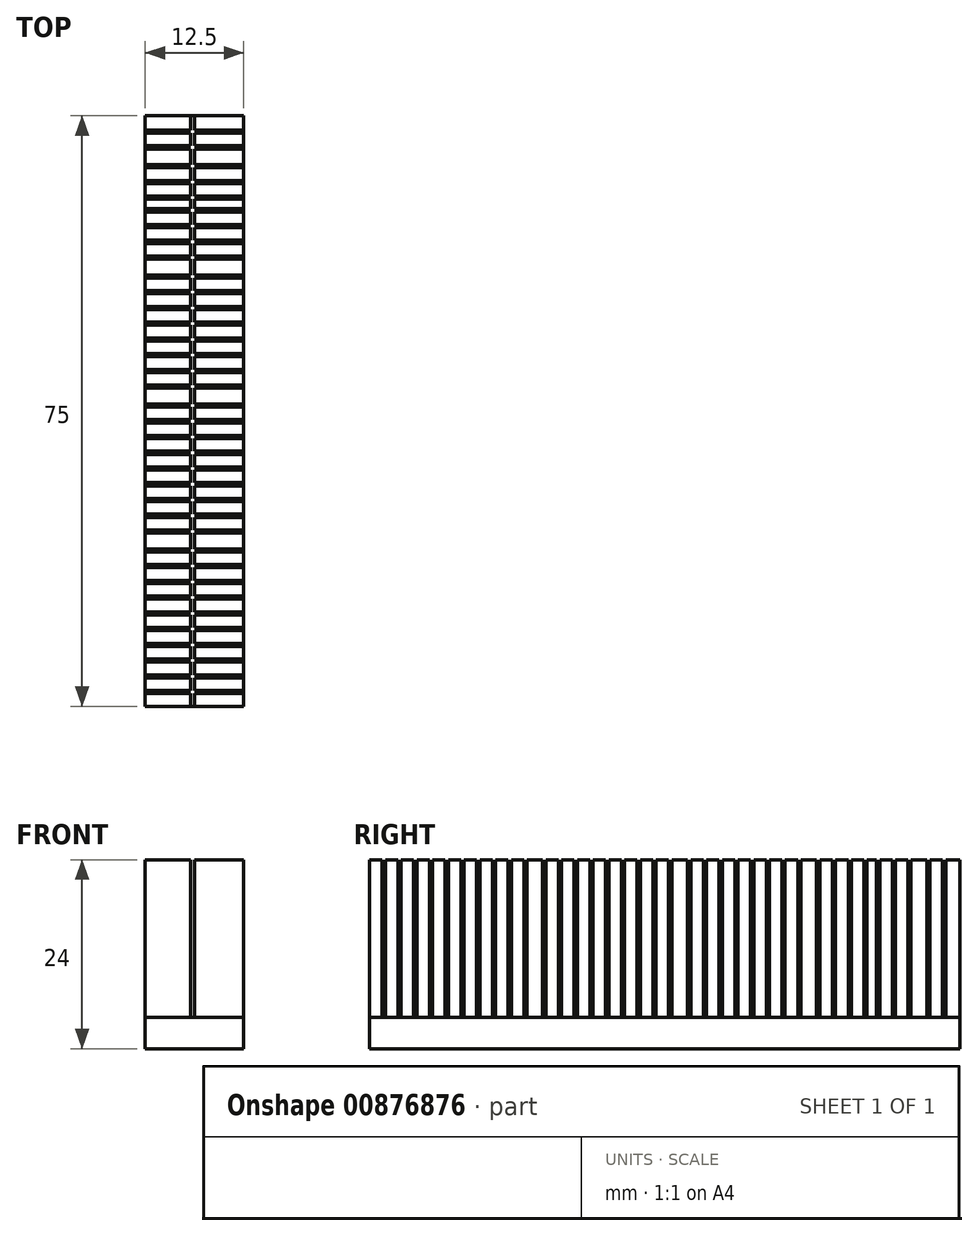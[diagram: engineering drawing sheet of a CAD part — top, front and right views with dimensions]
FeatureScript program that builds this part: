
annotation { "Feature Type Name" : "Feature", "Feature Type Description" : "" }
export const myFeature = defineFeature(function(context is Context, id is Id, definition is map)
    precondition{}
    {
        {
            var Q0;
            Q0=qCreatedBy(makeId("Top.planeOp"),FACE);
            var sketch = newSketch(context, id + "F0", { "sketchPlane" : qUnion([Q0])});
            skLineSegment(sketch, "E0.bottom", {"start": v(6.25, 37.5) * mm, "end": v(-6.25, 37.5) * mm});
            skLineSegment(sketch, "E0.top", {"start": v(6.25, -37.5) * mm, "end": v(-6.25, -37.5) * mm});
            skLineSegment(sketch, "E0.left", {"start": v(6.25, 37.5) * mm, "end": v(6.25, -37.5) * mm});
            skLineSegment(sketch, "E0.right", {"start": v(-6.25, 37.5) * mm, "end": v(-6.25, -37.5) * mm});
            skPoint(sketch, "E0.middle", {"position": v(0, 0) * mm});
            skLineSegment(sketch, "E1", {"start": v(0, -37.5) * mm, "end": v(0, 37.5) * mm});
            skPoint(sketch, "E2", {"position": v(-0.5, -37.5) * mm});
            skLineSegment(sketch, "E3", {"start": v(-0.5, -37.5) * mm, "end": v(-0.5, 37.5) * mm});
            skLineSegment(sketch, "E4", {"start": v(-6.25, -35.9) * mm, "end": v(6.25, -35.9) * mm});
            skLineSegment(sketch, "E5", {"start": v(-6.25, -35.5) * mm, "end": v(6.25, -35.5) * mm});
            skLineSegment(sketch, "E6", {"start": v(-6.25, -33.9) * mm, "end": v(6.25, -33.9) * mm});
            skLineSegment(sketch, "E7", {"start": v(-6.25, -33.5) * mm, "end": v(6.25, -33.5) * mm});
            skLineSegment(sketch, "E8", {"start": v(-6.25, -31.9) * mm, "end": v(6.25, -31.9) * mm});
            skLineSegment(sketch, "E9", {"start": v(-6.25, -31.5) * mm, "end": v(6.25, -31.5) * mm});
            skLineSegment(sketch, "E10", {"start": v(-6.25, -29.9) * mm, "end": v(6.25, -29.9) * mm});
            skLineSegment(sketch, "E11", {"start": v(-6.25, -29.5) * mm, "end": v(6.25, -29.5) * mm});
            skLineSegment(sketch, "E12", {"start": v(-6.25, -25.9) * mm, "end": v(6.25, -25.9) * mm});
            skLineSegment(sketch, "E13", {"start": v(-6.25, -23.5) * mm, "end": v(6.25, -23.5) * mm});
            skLineSegment(sketch, "E14", {"start": v(-6.25, -21.9) * mm, "end": v(6.25, -21.9) * mm});
            skLineSegment(sketch, "E15", {"start": v(-6.25, -21.5) * mm, "end": v(6.25, -21.5) * mm});
            skLineSegment(sketch, "E16", {"start": v(-6.25, -19.9) * mm, "end": v(6.25, -19.9) * mm});
            skLineSegment(sketch, "E17", {"start": v(-6.25, -19.5) * mm, "end": v(6.25, -19.5) * mm});
            skLineSegment(sketch, "E18", {"start": v(-6.25, -17.9) * mm, "end": v(6.25, -17.9) * mm});
            skLineSegment(sketch, "E19", {"start": v(-6.25, -17.5) * mm, "end": v(6.25, -17.5) * mm});
            skLineSegment(sketch, "E20", {"start": v(-6.25, -23.9) * mm, "end": v(6.25, -23.9) * mm});
            skLineSegment(sketch, "E21", {"start": v(-6.25, -25.5) * mm, "end": v(6.25, -25.5) * mm});
            skLineSegment(sketch, "E22", {"start": v(-6.25, -27.5) * mm, "end": v(6.25, -27.5) * mm});
            skLineSegment(sketch, "E23", {"start": v(-6.25, -27.9) * mm, "end": v(6.25, -27.9) * mm});
            skLineSegment(sketch, "E24.MirrorCS", {"start": v(-6.25, -15.1) * mm, "end": v(6.25, -15.1) * mm});
            skLineSegment(sketch, "E25.MirrorCS", {"start": v(-6.25, -15.5) * mm, "end": v(6.25, -15.5) * mm});
            skLineSegment(sketch, "E26.MirrorCS", {"start": v(-6.25, -13.1) * mm, "end": v(6.25, -13.1) * mm});
            skLineSegment(sketch, "E27.MirrorCS", {"start": v(-6.25, -13.5) * mm, "end": v(6.25, -13.5) * mm});
            skLineSegment(sketch, "E28.MirrorCS", {"start": v(-6.25, -11.1) * mm, "end": v(6.25, -11.1) * mm});
            skLineSegment(sketch, "E29.MirrorCS", {"start": v(-6.25, -11.5) * mm, "end": v(6.25, -11.5) * mm});
            skLineSegment(sketch, "E30.MirrorCS", {"start": v(-6.25, -9.1) * mm, "end": v(6.25, -9.1) * mm});
            skLineSegment(sketch, "E31.MirrorCS", {"start": v(-6.25, -9.5) * mm, "end": v(6.25, -9.5) * mm});
            skLineSegment(sketch, "E32.MirrorCS", {"start": v(-6.25, -7.5) * mm, "end": v(6.25, -7.5) * mm});
            skLineSegment(sketch, "E33.MirrorCS", {"start": v(-6.25, -7.1) * mm, "end": v(6.25, -7.1) * mm});
            skLineSegment(sketch, "E34.MirrorCS", {"start": v(-6.25, -5.5) * mm, "end": v(6.25, -5.5) * mm});
            skLineSegment(sketch, "E35.MirrorCS", {"start": v(-6.25, -5.1) * mm, "end": v(6.25, -5.1) * mm});
            skLineSegment(sketch, "E36.MirrorCS", {"start": v(-6.25, -3.5) * mm, "end": v(6.25, -3.5) * mm});
            skLineSegment(sketch, "E37.MirrorCS", {"start": v(-6.25, -3.1) * mm, "end": v(6.25, -3.1) * mm});
            skLineSegment(sketch, "E38.MirrorCS", {"start": v(-6.25, -1.1) * mm, "end": v(6.25, -1.1) * mm});
            skLineSegment(sketch, "E39.MirrorCS", {"start": v(-6.25, -1.5) * mm, "end": v(6.25, -1.5) * mm});
            skLineSegment(sketch, "E40.MirrorCS", {"start": v(-6.25, 0.5) * mm, "end": v(6.25, 0.5) * mm});
            skLineSegment(sketch, "E41.MirrorCS", {"start": v(-6.25, 0.9) * mm, "end": v(6.25, 0.9) * mm});
            skLineSegment(sketch, "E42.MirrorCS", {"start": v(-6.25, 2.9) * mm, "end": v(6.25, 2.9) * mm});
            skLineSegment(sketch, "E43.MirrorCS", {"start": v(-6.25, 3.3) * mm, "end": v(6.25, 3.3) * mm});
            skLineSegment(sketch, "E44.MirrorCS", {"start": v(-6.25, 5.3) * mm, "end": v(6.25, 5.3) * mm});
            skLineSegment(sketch, "E45.MirrorCS", {"start": v(-6.25, 4.9) * mm, "end": v(6.25, 4.9) * mm});
            skLineSegment(sketch, "E46.MirrorCS", {"start": v(-6.25, 6.9) * mm, "end": v(6.25, 6.9) * mm});
            skLineSegment(sketch, "E47.MirrorCS", {"start": v(-6.25, 7.3) * mm, "end": v(6.25, 7.3) * mm});
            skLineSegment(sketch, "E48.MirrorCS", {"start": v(-6.25, 8.9) * mm, "end": v(6.25, 8.9) * mm});
            skLineSegment(sketch, "E49.MirrorCS", {"start": v(-6.25, 9.3) * mm, "end": v(6.25, 9.3) * mm});
            skLineSegment(sketch, "E50.MirrorCS", {"start": v(-6.25, 10.9) * mm, "end": v(6.25, 10.9) * mm});
            skLineSegment(sketch, "E51.MirrorCS", {"start": v(-6.25, 11.3) * mm, "end": v(6.25, 11.3) * mm});
            skLineSegment(sketch, "E52.MirrorCS", {"start": v(-6.25, 12.9) * mm, "end": v(6.25, 12.9) * mm});
            skLineSegment(sketch, "E53.MirrorCS", {"start": v(-6.25, 13.3) * mm, "end": v(6.25, 13.3) * mm});
            skLineSegment(sketch, "E54.MirrorCS", {"start": v(-6.25, 14.9) * mm, "end": v(6.25, 14.9) * mm});
            skLineSegment(sketch, "E55.MirrorCS", {"start": v(-6.25, 15.3) * mm, "end": v(6.25, 15.3) * mm});
            skLineSegment(sketch, "E56.MirrorCS", {"start": v(-6.25, 16.9) * mm, "end": v(6.25, 16.9) * mm});
            skLineSegment(sketch, "E57.MirrorCS", {"start": v(-6.25, 17.3) * mm, "end": v(6.25, 17.3) * mm});
            skLineSegment(sketch, "E58.MirrorCS", {"start": v(-6.25, 19.7) * mm, "end": v(6.25, 19.7) * mm});
            skLineSegment(sketch, "E59.MirrorCS", {"start": v(-6.25, 19.3) * mm, "end": v(6.25, 19.3) * mm});
            skLineSegment(sketch, "E60.MirrorCS", {"start": v(-6.25, 21.3) * mm, "end": v(6.25, 21.3) * mm});
            skLineSegment(sketch, "E61.MirrorCS", {"start": v(-6.25, 21.7) * mm, "end": v(6.25, 21.7) * mm});
            skLineSegment(sketch, "E62.MirrorCS", {"start": v(-6.25, 23.3) * mm, "end": v(6.25, 23.3) * mm});
            skLineSegment(sketch, "E63.MirrorCS", {"start": v(-6.25, 23.7) * mm, "end": v(6.25, 23.7) * mm});
            skLineSegment(sketch, "E64.MirrorCS", {"start": v(-6.25, 25.7) * mm, "end": v(6.25, 25.7) * mm});
            skLineSegment(sketch, "E65.MirrorCS", {"start": v(-6.25, 25.3) * mm, "end": v(6.25, 25.3) * mm});
            skLineSegment(sketch, "E66.MirrorCS", {"start": v(-6.25, 26.9) * mm, "end": v(6.25, 26.9) * mm});
            skLineSegment(sketch, "E67.MirrorCS", {"start": v(-6.25, 27.3) * mm, "end": v(6.25, 27.3) * mm});
            skLineSegment(sketch, "E68.MirrorCS", {"start": v(-6.25, 28.9) * mm, "end": v(6.25, 28.9) * mm});
            skLineSegment(sketch, "E69.MirrorCS", {"start": v(-6.25, 29.3) * mm, "end": v(6.25, 29.3) * mm});
            skLineSegment(sketch, "E70.MirrorCS", {"start": v(-6.25, 30.9) * mm, "end": v(6.25, 30.9) * mm});
            skLineSegment(sketch, "E71.MirrorCS", {"start": v(-6.25, 31.3) * mm, "end": v(6.25, 31.3) * mm});
            skLineSegment(sketch, "E72.MirrorCS", {"start": v(-6.25, 33.3) * mm, "end": v(6.25, 33.3) * mm});
            skLineSegment(sketch, "E73.MirrorCS", {"start": v(-6.25, 33.7) * mm, "end": v(6.25, 33.7) * mm});
            skLineSegment(sketch, "E74.MirrorCS", {"start": v(-6.25, 35.7) * mm, "end": v(6.25, 35.7) * mm});
            skLineSegment(sketch, "E75.MirrorCS", {"start": v(-6.25, 35.3) * mm, "end": v(6.25, 35.3) * mm});
            skSolve(sketch);
        }
        {
            var Q0;
            {var subQ0=sQuery(id+"F0.wireOp",EDGE,"E0.left");var subQ1=sQuery(id+"F0.wireOp",EDGE,"E0.bottom");var subQ2=makeQuery(id+"F0.imprint","INTERSECT",VERTEX,{"derivedFrom":[subQ1,subQ0]});Q0=makeQuery(id+"F0.imprint","IMPRINT",FACE,{"disambiguationData":[TD([[makeQuery(id+"F0.imprint","IMPRINT",EDGE,{"disambiguationData":[TD([[subQ2,-1.0]])],"derivedFrom":subQ1}),1.0]])]});}
            var Q1;
            {var subQ0=sQuery(id+"F0.wireOp",EDGE,"E0.right");var subQ1=sQuery(id+"F0.wireOp",EDGE,"E0.bottom");var subQ2=makeQuery(id+"F0.imprint","INTERSECT",VERTEX,{"derivedFrom":[subQ1,subQ0]});Q1=makeQuery(id+"F0.imprint","IMPRINT",FACE,{"disambiguationData":[TD([[makeQuery(id+"F0.imprint","IMPRINT",EDGE,{"disambiguationData":[TD([[subQ2,1.0]])],"derivedFrom":subQ1}),1.0]])]});}
            var Q2;
            {var subQ0=sQuery(id+"F0.wireOp",EDGE,"E73.MirrorCS");var subQ1=sQuery(id+"F0.wireOp",EDGE,"E0.left");var subQ2=makeQuery(id+"F0.imprint","INTERSECT",VERTEX,{"derivedFrom":[subQ1,subQ0]});Q2=makeQuery(id+"F0.imprint","IMPRINT",FACE,{"disambiguationData":[TD([[makeQuery(id+"F0.imprint","IMPRINT",EDGE,{"disambiguationData":[TD([[subQ2,1.0]])],"derivedFrom":subQ1}),-1.0]])]});}
            var Q3;
            {var subQ0=sQuery(id+"F0.wireOp",EDGE,"E73.MirrorCS");var subQ1=sQuery(id+"F0.wireOp",EDGE,"E0.right");var subQ2=makeQuery(id+"F0.imprint","INTERSECT",VERTEX,{"derivedFrom":[subQ1,subQ0]});Q3=makeQuery(id+"F0.imprint","IMPRINT",FACE,{"disambiguationData":[TD([[makeQuery(id+"F0.imprint","IMPRINT",EDGE,{"disambiguationData":[TD([[subQ2,1.0]])],"derivedFrom":subQ1}),1.0]])]});}
            var Q4;
            {var subQ0=sQuery(id+"F0.wireOp",EDGE,"E71.MirrorCS");var subQ1=sQuery(id+"F0.wireOp",EDGE,"E0.left");var subQ2=makeQuery(id+"F0.imprint","INTERSECT",VERTEX,{"derivedFrom":[subQ1,subQ0]});Q4=makeQuery(id+"F0.imprint","IMPRINT",FACE,{"disambiguationData":[TD([[makeQuery(id+"F0.imprint","IMPRINT",EDGE,{"disambiguationData":[TD([[subQ2,1.0]])],"derivedFrom":subQ1}),-1.0]])]});}
            var Q5;
            {var subQ0=sQuery(id+"F0.wireOp",EDGE,"E71.MirrorCS");var subQ1=sQuery(id+"F0.wireOp",EDGE,"E0.right");var subQ2=makeQuery(id+"F0.imprint","INTERSECT",VERTEX,{"derivedFrom":[subQ1,subQ0]});Q5=makeQuery(id+"F0.imprint","IMPRINT",FACE,{"disambiguationData":[TD([[makeQuery(id+"F0.imprint","IMPRINT",EDGE,{"disambiguationData":[TD([[subQ2,1.0]])],"derivedFrom":subQ1}),1.0]])]});}
            var Q6;
            {var subQ0=sQuery(id+"F0.wireOp",EDGE,"E69.MirrorCS");var subQ1=sQuery(id+"F0.wireOp",EDGE,"E0.right");var subQ2=makeQuery(id+"F0.imprint","INTERSECT",VERTEX,{"derivedFrom":[subQ1,subQ0]});Q6=makeQuery(id+"F0.imprint","IMPRINT",FACE,{"disambiguationData":[TD([[makeQuery(id+"F0.imprint","IMPRINT",EDGE,{"disambiguationData":[TD([[subQ2,1.0]])],"derivedFrom":subQ1}),1.0]])]});}
            var Q7;
            {var subQ0=sQuery(id+"F0.wireOp",EDGE,"E69.MirrorCS");var subQ1=sQuery(id+"F0.wireOp",EDGE,"E0.left");var subQ2=makeQuery(id+"F0.imprint","INTERSECT",VERTEX,{"derivedFrom":[subQ1,subQ0]});Q7=makeQuery(id+"F0.imprint","IMPRINT",FACE,{"disambiguationData":[TD([[makeQuery(id+"F0.imprint","IMPRINT",EDGE,{"disambiguationData":[TD([[subQ2,1.0]])],"derivedFrom":subQ1}),-1.0]])]});}
            var Q8;
            {var subQ0=sQuery(id+"F0.wireOp",EDGE,"E67.MirrorCS");var subQ1=sQuery(id+"F0.wireOp",EDGE,"E0.left");var subQ2=makeQuery(id+"F0.imprint","INTERSECT",VERTEX,{"derivedFrom":[subQ1,subQ0]});Q8=makeQuery(id+"F0.imprint","IMPRINT",FACE,{"disambiguationData":[TD([[makeQuery(id+"F0.imprint","IMPRINT",EDGE,{"disambiguationData":[TD([[subQ2,1.0]])],"derivedFrom":subQ1}),-1.0]])]});}
            var Q9;
            {var subQ0=sQuery(id+"F0.wireOp",EDGE,"E67.MirrorCS");var subQ1=sQuery(id+"F0.wireOp",EDGE,"E0.right");var subQ2=makeQuery(id+"F0.imprint","INTERSECT",VERTEX,{"derivedFrom":[subQ1,subQ0]});Q9=makeQuery(id+"F0.imprint","IMPRINT",FACE,{"disambiguationData":[TD([[makeQuery(id+"F0.imprint","IMPRINT",EDGE,{"disambiguationData":[TD([[subQ2,1.0]])],"derivedFrom":subQ1}),1.0]])]});}
            var Q10;
            {var subQ0=sQuery(id+"F0.wireOp",EDGE,"E64.MirrorCS");var subQ1=sQuery(id+"F0.wireOp",EDGE,"E0.right");var subQ2=makeQuery(id+"F0.imprint","INTERSECT",VERTEX,{"derivedFrom":[subQ1,subQ0]});Q10=makeQuery(id+"F0.imprint","IMPRINT",FACE,{"disambiguationData":[TD([[makeQuery(id+"F0.imprint","IMPRINT",EDGE,{"disambiguationData":[TD([[subQ2,1.0]])],"derivedFrom":subQ1}),1.0]])]});}
            var Q11;
            {var subQ0=sQuery(id+"F0.wireOp",EDGE,"E64.MirrorCS");var subQ1=sQuery(id+"F0.wireOp",EDGE,"E0.left");var subQ2=makeQuery(id+"F0.imprint","INTERSECT",VERTEX,{"derivedFrom":[subQ1,subQ0]});Q11=makeQuery(id+"F0.imprint","IMPRINT",FACE,{"disambiguationData":[TD([[makeQuery(id+"F0.imprint","IMPRINT",EDGE,{"disambiguationData":[TD([[subQ2,1.0]])],"derivedFrom":subQ1}),-1.0]])]});}
            var Q12;
            {var subQ0=sQuery(id+"F0.wireOp",EDGE,"E63.MirrorCS");var subQ1=sQuery(id+"F0.wireOp",EDGE,"E0.right");var subQ2=makeQuery(id+"F0.imprint","INTERSECT",VERTEX,{"derivedFrom":[subQ1,subQ0]});Q12=makeQuery(id+"F0.imprint","IMPRINT",FACE,{"disambiguationData":[TD([[makeQuery(id+"F0.imprint","IMPRINT",EDGE,{"disambiguationData":[TD([[subQ2,1.0]])],"derivedFrom":subQ1}),1.0]])]});}
            var Q13;
            {var subQ0=sQuery(id+"F0.wireOp",EDGE,"E63.MirrorCS");var subQ1=sQuery(id+"F0.wireOp",EDGE,"E0.left");var subQ2=makeQuery(id+"F0.imprint","INTERSECT",VERTEX,{"derivedFrom":[subQ1,subQ0]});Q13=makeQuery(id+"F0.imprint","IMPRINT",FACE,{"disambiguationData":[TD([[makeQuery(id+"F0.imprint","IMPRINT",EDGE,{"disambiguationData":[TD([[subQ2,1.0]])],"derivedFrom":subQ1}),-1.0]])]});}
            var Q14;
            {var subQ0=sQuery(id+"F0.wireOp",EDGE,"E61.MirrorCS");var subQ1=sQuery(id+"F0.wireOp",EDGE,"E0.right");var subQ2=makeQuery(id+"F0.imprint","INTERSECT",VERTEX,{"derivedFrom":[subQ1,subQ0]});Q14=makeQuery(id+"F0.imprint","IMPRINT",FACE,{"disambiguationData":[TD([[makeQuery(id+"F0.imprint","IMPRINT",EDGE,{"disambiguationData":[TD([[subQ2,1.0]])],"derivedFrom":subQ1}),1.0]])]});}
            var Q15;
            {var subQ0=sQuery(id+"F0.wireOp",EDGE,"E61.MirrorCS");var subQ1=sQuery(id+"F0.wireOp",EDGE,"E0.left");var subQ2=makeQuery(id+"F0.imprint","INTERSECT",VERTEX,{"derivedFrom":[subQ1,subQ0]});Q15=makeQuery(id+"F0.imprint","IMPRINT",FACE,{"disambiguationData":[TD([[makeQuery(id+"F0.imprint","IMPRINT",EDGE,{"disambiguationData":[TD([[subQ2,1.0]])],"derivedFrom":subQ1}),-1.0]])]});}
            var Q16;
            {var subQ0=sQuery(id+"F0.wireOp",EDGE,"E60.MirrorCS");var subQ1=sQuery(id+"F0.wireOp",EDGE,"E0.right");var subQ2=makeQuery(id+"F0.imprint","INTERSECT",VERTEX,{"derivedFrom":[subQ1,subQ0]});Q16=makeQuery(id+"F0.imprint","IMPRINT",FACE,{"disambiguationData":[TD([[makeQuery(id+"F0.imprint","IMPRINT",EDGE,{"disambiguationData":[TD([[subQ2,-1.0]])],"derivedFrom":subQ1}),1.0]])]});}
            var Q17;
            {var subQ0=sQuery(id+"F0.wireOp",EDGE,"E60.MirrorCS");var subQ1=sQuery(id+"F0.wireOp",EDGE,"E0.left");var subQ2=makeQuery(id+"F0.imprint","INTERSECT",VERTEX,{"derivedFrom":[subQ1,subQ0]});Q17=makeQuery(id+"F0.imprint","IMPRINT",FACE,{"disambiguationData":[TD([[makeQuery(id+"F0.imprint","IMPRINT",EDGE,{"disambiguationData":[TD([[subQ2,-1.0]])],"derivedFrom":subQ1}),-1.0]])]});}
            var Q18;
            {var subQ0=sQuery(id+"F0.wireOp",EDGE,"E57.MirrorCS");var subQ1=sQuery(id+"F0.wireOp",EDGE,"E0.right");var subQ2=makeQuery(id+"F0.imprint","INTERSECT",VERTEX,{"derivedFrom":[subQ1,subQ0]});Q18=makeQuery(id+"F0.imprint","IMPRINT",FACE,{"disambiguationData":[TD([[makeQuery(id+"F0.imprint","IMPRINT",EDGE,{"disambiguationData":[TD([[subQ2,1.0]])],"derivedFrom":subQ1}),1.0]])]});}
            var Q19;
            {var subQ0=sQuery(id+"F0.wireOp",EDGE,"E57.MirrorCS");var subQ1=sQuery(id+"F0.wireOp",EDGE,"E0.left");var subQ2=makeQuery(id+"F0.imprint","INTERSECT",VERTEX,{"derivedFrom":[subQ1,subQ0]});Q19=makeQuery(id+"F0.imprint","IMPRINT",FACE,{"disambiguationData":[TD([[makeQuery(id+"F0.imprint","IMPRINT",EDGE,{"disambiguationData":[TD([[subQ2,1.0]])],"derivedFrom":subQ1}),-1.0]])]});}
            var Q20;
            {var subQ0=sQuery(id+"F0.wireOp",EDGE,"E55.MirrorCS");var subQ1=sQuery(id+"F0.wireOp",EDGE,"E0.left");var subQ2=makeQuery(id+"F0.imprint","INTERSECT",VERTEX,{"derivedFrom":[subQ1,subQ0]});Q20=makeQuery(id+"F0.imprint","IMPRINT",FACE,{"disambiguationData":[TD([[makeQuery(id+"F0.imprint","IMPRINT",EDGE,{"disambiguationData":[TD([[subQ2,1.0]])],"derivedFrom":subQ1}),-1.0]])]});}
            var Q21;
            {var subQ0=sQuery(id+"F0.wireOp",EDGE,"E55.MirrorCS");var subQ1=sQuery(id+"F0.wireOp",EDGE,"E0.right");var subQ2=makeQuery(id+"F0.imprint","INTERSECT",VERTEX,{"derivedFrom":[subQ1,subQ0]});Q21=makeQuery(id+"F0.imprint","IMPRINT",FACE,{"disambiguationData":[TD([[makeQuery(id+"F0.imprint","IMPRINT",EDGE,{"disambiguationData":[TD([[subQ2,1.0]])],"derivedFrom":subQ1}),1.0]])]});}
            var Q22;
            {var subQ0=sQuery(id+"F0.wireOp",EDGE,"E53.MirrorCS");var subQ1=sQuery(id+"F0.wireOp",EDGE,"E0.left");var subQ2=makeQuery(id+"F0.imprint","INTERSECT",VERTEX,{"derivedFrom":[subQ1,subQ0]});Q22=makeQuery(id+"F0.imprint","IMPRINT",FACE,{"disambiguationData":[TD([[makeQuery(id+"F0.imprint","IMPRINT",EDGE,{"disambiguationData":[TD([[subQ2,1.0]])],"derivedFrom":subQ1}),-1.0]])]});}
            var Q23;
            {var subQ0=sQuery(id+"F0.wireOp",EDGE,"E53.MirrorCS");var subQ1=sQuery(id+"F0.wireOp",EDGE,"E0.right");var subQ2=makeQuery(id+"F0.imprint","INTERSECT",VERTEX,{"derivedFrom":[subQ1,subQ0]});Q23=makeQuery(id+"F0.imprint","IMPRINT",FACE,{"disambiguationData":[TD([[makeQuery(id+"F0.imprint","IMPRINT",EDGE,{"disambiguationData":[TD([[subQ2,1.0]])],"derivedFrom":subQ1}),1.0]])]});}
            var Q24;
            {var subQ0=sQuery(id+"F0.wireOp",EDGE,"E51.MirrorCS");var subQ1=sQuery(id+"F0.wireOp",EDGE,"E0.right");var subQ2=makeQuery(id+"F0.imprint","INTERSECT",VERTEX,{"derivedFrom":[subQ1,subQ0]});Q24=makeQuery(id+"F0.imprint","IMPRINT",FACE,{"disambiguationData":[TD([[makeQuery(id+"F0.imprint","IMPRINT",EDGE,{"disambiguationData":[TD([[subQ2,1.0]])],"derivedFrom":subQ1}),1.0]])]});}
            var Q25;
            {var subQ0=sQuery(id+"F0.wireOp",EDGE,"E51.MirrorCS");var subQ1=sQuery(id+"F0.wireOp",EDGE,"E0.left");var subQ2=makeQuery(id+"F0.imprint","INTERSECT",VERTEX,{"derivedFrom":[subQ1,subQ0]});Q25=makeQuery(id+"F0.imprint","IMPRINT",FACE,{"disambiguationData":[TD([[makeQuery(id+"F0.imprint","IMPRINT",EDGE,{"disambiguationData":[TD([[subQ2,1.0]])],"derivedFrom":subQ1}),-1.0]])]});}
            var Q26;
            {var subQ0=sQuery(id+"F0.wireOp",EDGE,"E49.MirrorCS");var subQ1=sQuery(id+"F0.wireOp",EDGE,"E0.right");var subQ2=makeQuery(id+"F0.imprint","INTERSECT",VERTEX,{"derivedFrom":[subQ1,subQ0]});Q26=makeQuery(id+"F0.imprint","IMPRINT",FACE,{"disambiguationData":[TD([[makeQuery(id+"F0.imprint","IMPRINT",EDGE,{"disambiguationData":[TD([[subQ2,1.0]])],"derivedFrom":subQ1}),1.0]])]});}
            var Q27;
            {var subQ0=sQuery(id+"F0.wireOp",EDGE,"E49.MirrorCS");var subQ1=sQuery(id+"F0.wireOp",EDGE,"E0.left");var subQ2=makeQuery(id+"F0.imprint","INTERSECT",VERTEX,{"derivedFrom":[subQ1,subQ0]});Q27=makeQuery(id+"F0.imprint","IMPRINT",FACE,{"disambiguationData":[TD([[makeQuery(id+"F0.imprint","IMPRINT",EDGE,{"disambiguationData":[TD([[subQ2,1.0]])],"derivedFrom":subQ1}),-1.0]])]});}
            var Q28;
            {var subQ0=sQuery(id+"F0.wireOp",EDGE,"E47.MirrorCS");var subQ1=sQuery(id+"F0.wireOp",EDGE,"E0.right");var subQ2=makeQuery(id+"F0.imprint","INTERSECT",VERTEX,{"derivedFrom":[subQ1,subQ0]});Q28=makeQuery(id+"F0.imprint","IMPRINT",FACE,{"disambiguationData":[TD([[makeQuery(id+"F0.imprint","IMPRINT",EDGE,{"disambiguationData":[TD([[subQ2,1.0]])],"derivedFrom":subQ1}),1.0]])]});}
            var Q29;
            {var subQ0=sQuery(id+"F0.wireOp",EDGE,"E47.MirrorCS");var subQ1=sQuery(id+"F0.wireOp",EDGE,"E0.left");var subQ2=makeQuery(id+"F0.imprint","INTERSECT",VERTEX,{"derivedFrom":[subQ1,subQ0]});Q29=makeQuery(id+"F0.imprint","IMPRINT",FACE,{"disambiguationData":[TD([[makeQuery(id+"F0.imprint","IMPRINT",EDGE,{"disambiguationData":[TD([[subQ2,1.0]])],"derivedFrom":subQ1}),-1.0]])]});}
            var Q30;
            {var subQ0=sQuery(id+"F0.wireOp",EDGE,"E44.MirrorCS");var subQ1=sQuery(id+"F0.wireOp",EDGE,"E0.left");var subQ2=makeQuery(id+"F0.imprint","INTERSECT",VERTEX,{"derivedFrom":[subQ1,subQ0]});Q30=makeQuery(id+"F0.imprint","IMPRINT",FACE,{"disambiguationData":[TD([[makeQuery(id+"F0.imprint","IMPRINT",EDGE,{"disambiguationData":[TD([[subQ2,1.0]])],"derivedFrom":subQ1}),-1.0]])]});}
            var Q31;
            {var subQ0=sQuery(id+"F0.wireOp",EDGE,"E44.MirrorCS");var subQ1=sQuery(id+"F0.wireOp",EDGE,"E0.right");var subQ2=makeQuery(id+"F0.imprint","INTERSECT",VERTEX,{"derivedFrom":[subQ1,subQ0]});Q31=makeQuery(id+"F0.imprint","IMPRINT",FACE,{"disambiguationData":[TD([[makeQuery(id+"F0.imprint","IMPRINT",EDGE,{"disambiguationData":[TD([[subQ2,1.0]])],"derivedFrom":subQ1}),1.0]])]});}
            var Q32;
            {var subQ0=sQuery(id+"F0.wireOp",EDGE,"E43.MirrorCS");var subQ1=sQuery(id+"F0.wireOp",EDGE,"E0.right");var subQ2=makeQuery(id+"F0.imprint","INTERSECT",VERTEX,{"derivedFrom":[subQ1,subQ0]});Q32=makeQuery(id+"F0.imprint","IMPRINT",FACE,{"disambiguationData":[TD([[makeQuery(id+"F0.imprint","IMPRINT",EDGE,{"disambiguationData":[TD([[subQ2,1.0]])],"derivedFrom":subQ1}),1.0]])]});}
            var Q33;
            {var subQ0=sQuery(id+"F0.wireOp",EDGE,"E43.MirrorCS");var subQ1=sQuery(id+"F0.wireOp",EDGE,"E0.left");var subQ2=makeQuery(id+"F0.imprint","INTERSECT",VERTEX,{"derivedFrom":[subQ1,subQ0]});Q33=makeQuery(id+"F0.imprint","IMPRINT",FACE,{"disambiguationData":[TD([[makeQuery(id+"F0.imprint","IMPRINT",EDGE,{"disambiguationData":[TD([[subQ2,1.0]])],"derivedFrom":subQ1}),-1.0]])]});}
            var Q34;
            {var subQ0=sQuery(id+"F0.wireOp",EDGE,"E41.MirrorCS");var subQ1=sQuery(id+"F0.wireOp",EDGE,"E0.left");var subQ2=makeQuery(id+"F0.imprint","INTERSECT",VERTEX,{"derivedFrom":[subQ1,subQ0]});Q34=makeQuery(id+"F0.imprint","IMPRINT",FACE,{"disambiguationData":[TD([[makeQuery(id+"F0.imprint","IMPRINT",EDGE,{"disambiguationData":[TD([[subQ2,1.0]])],"derivedFrom":subQ1}),-1.0]])]});}
            var Q35;
            {var subQ0=sQuery(id+"F0.wireOp",EDGE,"E41.MirrorCS");var subQ1=sQuery(id+"F0.wireOp",EDGE,"E0.right");var subQ2=makeQuery(id+"F0.imprint","INTERSECT",VERTEX,{"derivedFrom":[subQ1,subQ0]});Q35=makeQuery(id+"F0.imprint","IMPRINT",FACE,{"disambiguationData":[TD([[makeQuery(id+"F0.imprint","IMPRINT",EDGE,{"disambiguationData":[TD([[subQ2,1.0]])],"derivedFrom":subQ1}),1.0]])]});}
            var Q36;
            {var subQ0=sQuery(id+"F0.wireOp",EDGE,"E38.MirrorCS");var subQ1=sQuery(id+"F0.wireOp",EDGE,"E0.right");var subQ2=makeQuery(id+"F0.imprint","INTERSECT",VERTEX,{"derivedFrom":[subQ1,subQ0]});Q36=makeQuery(id+"F0.imprint","IMPRINT",FACE,{"disambiguationData":[TD([[makeQuery(id+"F0.imprint","IMPRINT",EDGE,{"disambiguationData":[TD([[subQ2,1.0]])],"derivedFrom":subQ1}),1.0]])]});}
            var Q37;
            {var subQ0=sQuery(id+"F0.wireOp",EDGE,"E38.MirrorCS");var subQ1=sQuery(id+"F0.wireOp",EDGE,"E0.left");var subQ2=makeQuery(id+"F0.imprint","INTERSECT",VERTEX,{"derivedFrom":[subQ1,subQ0]});Q37=makeQuery(id+"F0.imprint","IMPRINT",FACE,{"disambiguationData":[TD([[makeQuery(id+"F0.imprint","IMPRINT",EDGE,{"disambiguationData":[TD([[subQ2,1.0]])],"derivedFrom":subQ1}),-1.0]])]});}
            var Q38;
            {var subQ0=sQuery(id+"F0.wireOp",EDGE,"E37.MirrorCS");var subQ1=sQuery(id+"F0.wireOp",EDGE,"E0.right");var subQ2=makeQuery(id+"F0.imprint","INTERSECT",VERTEX,{"derivedFrom":[subQ1,subQ0]});Q38=makeQuery(id+"F0.imprint","IMPRINT",FACE,{"disambiguationData":[TD([[makeQuery(id+"F0.imprint","IMPRINT",EDGE,{"disambiguationData":[TD([[subQ2,1.0]])],"derivedFrom":subQ1}),1.0]])]});}
            var Q39;
            {var subQ0=sQuery(id+"F0.wireOp",EDGE,"E37.MirrorCS");var subQ1=sQuery(id+"F0.wireOp",EDGE,"E0.left");var subQ2=makeQuery(id+"F0.imprint","INTERSECT",VERTEX,{"derivedFrom":[subQ1,subQ0]});Q39=makeQuery(id+"F0.imprint","IMPRINT",FACE,{"disambiguationData":[TD([[makeQuery(id+"F0.imprint","IMPRINT",EDGE,{"disambiguationData":[TD([[subQ2,1.0]])],"derivedFrom":subQ1}),-1.0]])]});}
            var Q40;
            {var subQ0=sQuery(id+"F0.wireOp",EDGE,"E35.MirrorCS");var subQ1=sQuery(id+"F0.wireOp",EDGE,"E0.right");var subQ2=makeQuery(id+"F0.imprint","INTERSECT",VERTEX,{"derivedFrom":[subQ1,subQ0]});Q40=makeQuery(id+"F0.imprint","IMPRINT",FACE,{"disambiguationData":[TD([[makeQuery(id+"F0.imprint","IMPRINT",EDGE,{"disambiguationData":[TD([[subQ2,1.0]])],"derivedFrom":subQ1}),1.0]])]});}
            var Q41;
            {var subQ0=sQuery(id+"F0.wireOp",EDGE,"E35.MirrorCS");var subQ1=sQuery(id+"F0.wireOp",EDGE,"E0.left");var subQ2=makeQuery(id+"F0.imprint","INTERSECT",VERTEX,{"derivedFrom":[subQ1,subQ0]});Q41=makeQuery(id+"F0.imprint","IMPRINT",FACE,{"disambiguationData":[TD([[makeQuery(id+"F0.imprint","IMPRINT",EDGE,{"disambiguationData":[TD([[subQ2,1.0]])],"derivedFrom":subQ1}),-1.0]])]});}
            var Q42;
            {var subQ0=sQuery(id+"F0.wireOp",EDGE,"E33.MirrorCS");var subQ1=sQuery(id+"F0.wireOp",EDGE,"E0.right");var subQ2=makeQuery(id+"F0.imprint","INTERSECT",VERTEX,{"derivedFrom":[subQ1,subQ0]});Q42=makeQuery(id+"F0.imprint","IMPRINT",FACE,{"disambiguationData":[TD([[makeQuery(id+"F0.imprint","IMPRINT",EDGE,{"disambiguationData":[TD([[subQ2,1.0]])],"derivedFrom":subQ1}),1.0]])]});}
            var Q43;
            {var subQ0=sQuery(id+"F0.wireOp",EDGE,"E33.MirrorCS");var subQ1=sQuery(id+"F0.wireOp",EDGE,"E0.left");var subQ2=makeQuery(id+"F0.imprint","INTERSECT",VERTEX,{"derivedFrom":[subQ1,subQ0]});Q43=makeQuery(id+"F0.imprint","IMPRINT",FACE,{"disambiguationData":[TD([[makeQuery(id+"F0.imprint","IMPRINT",EDGE,{"disambiguationData":[TD([[subQ2,1.0]])],"derivedFrom":subQ1}),-1.0]])]});}
            var Q44;
            {var subQ0=sQuery(id+"F0.wireOp",EDGE,"E30.MirrorCS");var subQ1=sQuery(id+"F0.wireOp",EDGE,"E0.right");var subQ2=makeQuery(id+"F0.imprint","INTERSECT",VERTEX,{"derivedFrom":[subQ1,subQ0]});Q44=makeQuery(id+"F0.imprint","IMPRINT",FACE,{"disambiguationData":[TD([[makeQuery(id+"F0.imprint","IMPRINT",EDGE,{"disambiguationData":[TD([[subQ2,1.0]])],"derivedFrom":subQ1}),1.0]])]});}
            var Q45;
            {var subQ0=sQuery(id+"F0.wireOp",EDGE,"E30.MirrorCS");var subQ1=sQuery(id+"F0.wireOp",EDGE,"E0.left");var subQ2=makeQuery(id+"F0.imprint","INTERSECT",VERTEX,{"derivedFrom":[subQ1,subQ0]});Q45=makeQuery(id+"F0.imprint","IMPRINT",FACE,{"disambiguationData":[TD([[makeQuery(id+"F0.imprint","IMPRINT",EDGE,{"disambiguationData":[TD([[subQ2,1.0]])],"derivedFrom":subQ1}),-1.0]])]});}
            var Q46;
            {var subQ0=sQuery(id+"F0.wireOp",EDGE,"E28.MirrorCS");var subQ1=sQuery(id+"F0.wireOp",EDGE,"E0.right");var subQ2=makeQuery(id+"F0.imprint","INTERSECT",VERTEX,{"derivedFrom":[subQ1,subQ0]});Q46=makeQuery(id+"F0.imprint","IMPRINT",FACE,{"disambiguationData":[TD([[makeQuery(id+"F0.imprint","IMPRINT",EDGE,{"disambiguationData":[TD([[subQ2,1.0]])],"derivedFrom":subQ1}),1.0]])]});}
            var Q47;
            {var subQ0=sQuery(id+"F0.wireOp",EDGE,"E28.MirrorCS");var subQ1=sQuery(id+"F0.wireOp",EDGE,"E0.left");var subQ2=makeQuery(id+"F0.imprint","INTERSECT",VERTEX,{"derivedFrom":[subQ1,subQ0]});Q47=makeQuery(id+"F0.imprint","IMPRINT",FACE,{"disambiguationData":[TD([[makeQuery(id+"F0.imprint","IMPRINT",EDGE,{"disambiguationData":[TD([[subQ2,1.0]])],"derivedFrom":subQ1}),-1.0]])]});}
            var Q48;
            {var subQ0=sQuery(id+"F0.wireOp",EDGE,"E26.MirrorCS");var subQ1=sQuery(id+"F0.wireOp",EDGE,"E0.right");var subQ2=makeQuery(id+"F0.imprint","INTERSECT",VERTEX,{"derivedFrom":[subQ1,subQ0]});Q48=makeQuery(id+"F0.imprint","IMPRINT",FACE,{"disambiguationData":[TD([[makeQuery(id+"F0.imprint","IMPRINT",EDGE,{"disambiguationData":[TD([[subQ2,1.0]])],"derivedFrom":subQ1}),1.0]])]});}
            var Q49;
            {var subQ0=sQuery(id+"F0.wireOp",EDGE,"E26.MirrorCS");var subQ1=sQuery(id+"F0.wireOp",EDGE,"E0.left");var subQ2=makeQuery(id+"F0.imprint","INTERSECT",VERTEX,{"derivedFrom":[subQ1,subQ0]});Q49=makeQuery(id+"F0.imprint","IMPRINT",FACE,{"disambiguationData":[TD([[makeQuery(id+"F0.imprint","IMPRINT",EDGE,{"disambiguationData":[TD([[subQ2,1.0]])],"derivedFrom":subQ1}),-1.0]])]});}
            var Q50;
            {var subQ0=sQuery(id+"F0.wireOp",EDGE,"E24.MirrorCS");var subQ1=sQuery(id+"F0.wireOp",EDGE,"E0.right");var subQ2=makeQuery(id+"F0.imprint","INTERSECT",VERTEX,{"derivedFrom":[subQ1,subQ0]});Q50=makeQuery(id+"F0.imprint","IMPRINT",FACE,{"disambiguationData":[TD([[makeQuery(id+"F0.imprint","IMPRINT",EDGE,{"disambiguationData":[TD([[subQ2,1.0]])],"derivedFrom":subQ1}),1.0]])]});}
            var Q51;
            {var subQ0=sQuery(id+"F0.wireOp",EDGE,"E24.MirrorCS");var subQ1=sQuery(id+"F0.wireOp",EDGE,"E0.left");var subQ2=makeQuery(id+"F0.imprint","INTERSECT",VERTEX,{"derivedFrom":[subQ1,subQ0]});Q51=makeQuery(id+"F0.imprint","IMPRINT",FACE,{"disambiguationData":[TD([[makeQuery(id+"F0.imprint","IMPRINT",EDGE,{"disambiguationData":[TD([[subQ2,1.0]])],"derivedFrom":subQ1}),-1.0]])]});}
            var Q52;
            {var subQ0=sQuery(id+"F0.wireOp",EDGE,"E19");var subQ1=sQuery(id+"F0.wireOp",EDGE,"E0.right");var subQ2=makeQuery(id+"F0.imprint","INTERSECT",VERTEX,{"derivedFrom":[subQ1,subQ0]});Q52=makeQuery(id+"F0.imprint","IMPRINT",FACE,{"disambiguationData":[TD([[makeQuery(id+"F0.imprint","IMPRINT",EDGE,{"disambiguationData":[TD([[subQ2,1.0]])],"derivedFrom":subQ1}),1.0]])]});}
            var Q53;
            {var subQ0=sQuery(id+"F0.wireOp",EDGE,"E19");var subQ1=sQuery(id+"F0.wireOp",EDGE,"E0.left");var subQ2=makeQuery(id+"F0.imprint","INTERSECT",VERTEX,{"derivedFrom":[subQ1,subQ0]});Q53=makeQuery(id+"F0.imprint","IMPRINT",FACE,{"disambiguationData":[TD([[makeQuery(id+"F0.imprint","IMPRINT",EDGE,{"disambiguationData":[TD([[subQ2,1.0]])],"derivedFrom":subQ1}),-1.0]])]});}
            var Q54;
            {var subQ0=sQuery(id+"F0.wireOp",EDGE,"E17");var subQ1=sQuery(id+"F0.wireOp",EDGE,"E0.right");var subQ2=makeQuery(id+"F0.imprint","INTERSECT",VERTEX,{"derivedFrom":[subQ1,subQ0]});Q54=makeQuery(id+"F0.imprint","IMPRINT",FACE,{"disambiguationData":[TD([[makeQuery(id+"F0.imprint","IMPRINT",EDGE,{"disambiguationData":[TD([[subQ2,1.0]])],"derivedFrom":subQ1}),1.0]])]});}
            var Q55;
            {var subQ0=sQuery(id+"F0.wireOp",EDGE,"E17");var subQ1=sQuery(id+"F0.wireOp",EDGE,"E0.left");var subQ2=makeQuery(id+"F0.imprint","INTERSECT",VERTEX,{"derivedFrom":[subQ1,subQ0]});Q55=makeQuery(id+"F0.imprint","IMPRINT",FACE,{"disambiguationData":[TD([[makeQuery(id+"F0.imprint","IMPRINT",EDGE,{"disambiguationData":[TD([[subQ2,1.0]])],"derivedFrom":subQ1}),-1.0]])]});}
            var Q56;
            {var subQ0=sQuery(id+"F0.wireOp",EDGE,"E15");var subQ1=sQuery(id+"F0.wireOp",EDGE,"E0.right");var subQ2=makeQuery(id+"F0.imprint","INTERSECT",VERTEX,{"derivedFrom":[subQ1,subQ0]});Q56=makeQuery(id+"F0.imprint","IMPRINT",FACE,{"disambiguationData":[TD([[makeQuery(id+"F0.imprint","IMPRINT",EDGE,{"disambiguationData":[TD([[subQ2,1.0]])],"derivedFrom":subQ1}),1.0]])]});}
            var Q57;
            {var subQ0=sQuery(id+"F0.wireOp",EDGE,"E15");var subQ1=sQuery(id+"F0.wireOp",EDGE,"E0.left");var subQ2=makeQuery(id+"F0.imprint","INTERSECT",VERTEX,{"derivedFrom":[subQ1,subQ0]});Q57=makeQuery(id+"F0.imprint","IMPRINT",FACE,{"disambiguationData":[TD([[makeQuery(id+"F0.imprint","IMPRINT",EDGE,{"disambiguationData":[TD([[subQ2,1.0]])],"derivedFrom":subQ1}),-1.0]])]});}
            var Q58;
            {var subQ0=sQuery(id+"F0.wireOp",EDGE,"E13");var subQ1=sQuery(id+"F0.wireOp",EDGE,"E0.right");var subQ2=makeQuery(id+"F0.imprint","INTERSECT",VERTEX,{"derivedFrom":[subQ1,subQ0]});Q58=makeQuery(id+"F0.imprint","IMPRINT",FACE,{"disambiguationData":[TD([[makeQuery(id+"F0.imprint","IMPRINT",EDGE,{"disambiguationData":[TD([[subQ2,1.0]])],"derivedFrom":subQ1}),1.0]])]});}
            var Q59;
            {var subQ0=sQuery(id+"F0.wireOp",EDGE,"E13");var subQ1=sQuery(id+"F0.wireOp",EDGE,"E0.left");var subQ2=makeQuery(id+"F0.imprint","INTERSECT",VERTEX,{"derivedFrom":[subQ1,subQ0]});Q59=makeQuery(id+"F0.imprint","IMPRINT",FACE,{"disambiguationData":[TD([[makeQuery(id+"F0.imprint","IMPRINT",EDGE,{"disambiguationData":[TD([[subQ2,1.0]])],"derivedFrom":subQ1}),-1.0]])]});}
            var Q60;
            {var subQ0=sQuery(id+"F0.wireOp",EDGE,"E20");var subQ1=sQuery(id+"F0.wireOp",EDGE,"E0.right");var subQ2=makeQuery(id+"F0.imprint","INTERSECT",VERTEX,{"derivedFrom":[subQ1,subQ0]});Q60=makeQuery(id+"F0.imprint","IMPRINT",FACE,{"disambiguationData":[TD([[makeQuery(id+"F0.imprint","IMPRINT",EDGE,{"disambiguationData":[TD([[subQ2,-1.0]])],"derivedFrom":subQ1}),1.0]])]});}
            var Q61;
            {var subQ0=sQuery(id+"F0.wireOp",EDGE,"E20");var subQ1=sQuery(id+"F0.wireOp",EDGE,"E0.left");var subQ2=makeQuery(id+"F0.imprint","INTERSECT",VERTEX,{"derivedFrom":[subQ1,subQ0]});Q61=makeQuery(id+"F0.imprint","IMPRINT",FACE,{"disambiguationData":[TD([[makeQuery(id+"F0.imprint","IMPRINT",EDGE,{"disambiguationData":[TD([[subQ2,-1.0]])],"derivedFrom":subQ1}),-1.0]])]});}
            var Q62;
            {var subQ0=sQuery(id+"F0.wireOp",EDGE,"E12");var subQ1=sQuery(id+"F0.wireOp",EDGE,"E0.left");var subQ2=makeQuery(id+"F0.imprint","INTERSECT",VERTEX,{"derivedFrom":[subQ1,subQ0]});Q62=makeQuery(id+"F0.imprint","IMPRINT",FACE,{"disambiguationData":[TD([[makeQuery(id+"F0.imprint","IMPRINT",EDGE,{"disambiguationData":[TD([[subQ2,-1.0]])],"derivedFrom":subQ1}),-1.0]])]});}
            var Q63;
            {var subQ0=sQuery(id+"F0.wireOp",EDGE,"E12");var subQ1=sQuery(id+"F0.wireOp",EDGE,"E0.right");var subQ2=makeQuery(id+"F0.imprint","INTERSECT",VERTEX,{"derivedFrom":[subQ1,subQ0]});Q63=makeQuery(id+"F0.imprint","IMPRINT",FACE,{"disambiguationData":[TD([[makeQuery(id+"F0.imprint","IMPRINT",EDGE,{"disambiguationData":[TD([[subQ2,-1.0]])],"derivedFrom":subQ1}),1.0]])]});}
            var Q64;
            {var subQ0=sQuery(id+"F0.wireOp",EDGE,"E11");var subQ1=sQuery(id+"F0.wireOp",EDGE,"E0.right");var subQ2=makeQuery(id+"F0.imprint","INTERSECT",VERTEX,{"derivedFrom":[subQ1,subQ0]});Q64=makeQuery(id+"F0.imprint","IMPRINT",FACE,{"disambiguationData":[TD([[makeQuery(id+"F0.imprint","IMPRINT",EDGE,{"disambiguationData":[TD([[subQ2,1.0]])],"derivedFrom":subQ1}),1.0]])]});}
            var Q65;
            {var subQ0=sQuery(id+"F0.wireOp",EDGE,"E11");var subQ1=sQuery(id+"F0.wireOp",EDGE,"E0.left");var subQ2=makeQuery(id+"F0.imprint","INTERSECT",VERTEX,{"derivedFrom":[subQ1,subQ0]});Q65=makeQuery(id+"F0.imprint","IMPRINT",FACE,{"disambiguationData":[TD([[makeQuery(id+"F0.imprint","IMPRINT",EDGE,{"disambiguationData":[TD([[subQ2,1.0]])],"derivedFrom":subQ1}),-1.0]])]});}
            var Q66;
            {var subQ0=sQuery(id+"F0.wireOp",EDGE,"E9");var subQ1=sQuery(id+"F0.wireOp",EDGE,"E0.right");var subQ2=makeQuery(id+"F0.imprint","INTERSECT",VERTEX,{"derivedFrom":[subQ1,subQ0]});Q66=makeQuery(id+"F0.imprint","IMPRINT",FACE,{"disambiguationData":[TD([[makeQuery(id+"F0.imprint","IMPRINT",EDGE,{"disambiguationData":[TD([[subQ2,1.0]])],"derivedFrom":subQ1}),1.0]])]});}
            var Q67;
            {var subQ0=sQuery(id+"F0.wireOp",EDGE,"E9");var subQ1=sQuery(id+"F0.wireOp",EDGE,"E0.left");var subQ2=makeQuery(id+"F0.imprint","INTERSECT",VERTEX,{"derivedFrom":[subQ1,subQ0]});Q67=makeQuery(id+"F0.imprint","IMPRINT",FACE,{"disambiguationData":[TD([[makeQuery(id+"F0.imprint","IMPRINT",EDGE,{"disambiguationData":[TD([[subQ2,1.0]])],"derivedFrom":subQ1}),-1.0]])]});}
            var Q68;
            {var subQ0=sQuery(id+"F0.wireOp",EDGE,"E7");var subQ1=sQuery(id+"F0.wireOp",EDGE,"E0.left");var subQ2=makeQuery(id+"F0.imprint","INTERSECT",VERTEX,{"derivedFrom":[subQ1,subQ0]});Q68=makeQuery(id+"F0.imprint","IMPRINT",FACE,{"disambiguationData":[TD([[makeQuery(id+"F0.imprint","IMPRINT",EDGE,{"disambiguationData":[TD([[subQ2,1.0]])],"derivedFrom":subQ1}),-1.0]])]});}
            var Q69;
            {var subQ0=sQuery(id+"F0.wireOp",EDGE,"E7");var subQ1=sQuery(id+"F0.wireOp",EDGE,"E0.right");var subQ2=makeQuery(id+"F0.imprint","INTERSECT",VERTEX,{"derivedFrom":[subQ1,subQ0]});Q69=makeQuery(id+"F0.imprint","IMPRINT",FACE,{"disambiguationData":[TD([[makeQuery(id+"F0.imprint","IMPRINT",EDGE,{"disambiguationData":[TD([[subQ2,1.0]])],"derivedFrom":subQ1}),1.0]])]});}
            var Q70;
            {var subQ0=sQuery(id+"F0.wireOp",EDGE,"E5");var subQ1=sQuery(id+"F0.wireOp",EDGE,"E0.right");var subQ2=makeQuery(id+"F0.imprint","INTERSECT",VERTEX,{"derivedFrom":[subQ1,subQ0]});Q70=makeQuery(id+"F0.imprint","IMPRINT",FACE,{"disambiguationData":[TD([[makeQuery(id+"F0.imprint","IMPRINT",EDGE,{"disambiguationData":[TD([[subQ2,1.0]])],"derivedFrom":subQ1}),1.0]])]});}
            var Q71;
            {var subQ0=sQuery(id+"F0.wireOp",EDGE,"E5");var subQ1=sQuery(id+"F0.wireOp",EDGE,"E0.left");var subQ2=makeQuery(id+"F0.imprint","INTERSECT",VERTEX,{"derivedFrom":[subQ1,subQ0]});Q71=makeQuery(id+"F0.imprint","IMPRINT",FACE,{"disambiguationData":[TD([[makeQuery(id+"F0.imprint","IMPRINT",EDGE,{"disambiguationData":[TD([[subQ2,1.0]])],"derivedFrom":subQ1}),-1.0]])]});}
            var Q72;
            {var subQ0=sQuery(id+"F0.wireOp",EDGE,"E0.left");var subQ1=sQuery(id+"F0.wireOp",EDGE,"E0.top");var subQ2=makeQuery(id+"F0.imprint","INTERSECT",VERTEX,{"derivedFrom":[subQ1,subQ0]});Q72=makeQuery(id+"F0.imprint","IMPRINT",FACE,{"disambiguationData":[TD([[makeQuery(id+"F0.imprint","IMPRINT",EDGE,{"disambiguationData":[TD([[subQ2,-1.0]])],"derivedFrom":subQ1}),-1.0]])]});}
            var Q73;
            {var subQ0=sQuery(id+"F0.wireOp",EDGE,"E0.right");var subQ1=sQuery(id+"F0.wireOp",EDGE,"E0.top");var subQ2=makeQuery(id+"F0.imprint","INTERSECT",VERTEX,{"derivedFrom":[subQ1,subQ0]});Q73=makeQuery(id+"F0.imprint","IMPRINT",FACE,{"disambiguationData":[TD([[makeQuery(id+"F0.imprint","IMPRINT",EDGE,{"disambiguationData":[TD([[subQ2,1.0]])],"derivedFrom":subQ1}),-1.0]])]});}
            extrude(context, id + "F1", {"entities" : qUnion([Q0, Q1, Q2, Q3, Q4, Q5, Q6, Q7, Q8, Q9, Q10, Q11, Q12, Q13, Q14, Q15, Q16, Q17, Q18, Q19, Q20, Q21, Q22, Q23, Q24, Q25, Q26, Q27, Q28, Q29, Q30, Q31, Q32, Q33, Q34, Q35, Q36, Q37, Q38, Q39, Q40, Q41, Q42, Q43, Q44, Q45, Q46, Q47, Q48, Q49, Q50, Q51, Q52, Q53, Q54, Q55, Q56, Q57, Q58, Q59, Q60, Q61, Q62, Q63, Q64, Q65, Q66, Q67, Q68, Q69, Q70, Q71, Q72, Q73]), "depth" : 20 * mm, "offsetDistance" : 25 * mm});
        }
        {
            var Q0;
            Q0=qCreatedBy(makeId("Top.planeOp"),FACE);
            var sketch = newSketch(context, id + "F2", { "sketchPlane" : qUnion([Q0])});
            skLineSegment(sketch, "E76.bottom", {"start": v(6.25, 37.5) * mm, "end": v(-6.25, 37.5) * mm});
            skLineSegment(sketch, "E76.top", {"start": v(6.25, -37.5) * mm, "end": v(-6.25, -37.5) * mm});
            skLineSegment(sketch, "E76.left", {"start": v(6.25, 37.5) * mm, "end": v(6.25, -37.5) * mm});
            skLineSegment(sketch, "E76.right", {"start": v(-6.25, 37.5) * mm, "end": v(-6.25, -37.5) * mm});
            skPoint(sketch, "E76.middle", {"position": v(0, 0) * mm});
            skSolve(sketch);
        }
        {
            var Q0;
            Q0 = qSketchRegion(id + "F2", true);
            extrude(context, id + "F3", {"entities" : qUnion([Q0]), "oppositeDirection" : true, "depth" : 4 * mm, "offsetDistance" : 25 * mm});
        }
    });
